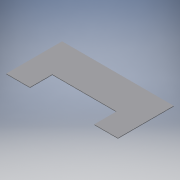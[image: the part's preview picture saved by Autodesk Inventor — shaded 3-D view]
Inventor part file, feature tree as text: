
AUTODESK INVENTOR PART (.ipt)
format: ipt  version: 2016 (Build 200138000, 138)  size: 108,544 bytes
history: native  units: mm
features: extrude x2, sketch x2
ambient origin geometry x8: Origin, YZ Plane, XZ Plane, XY Plane, X Axis, Y Axis, Z Axis, Center Point
bodies: Solid1 (feature_tree)
feature tree (4):
  extrude  "Extrusion1"  Depth=10.0mm TaperAngle=0.0deg
  extrude  "Extrusion2"  [1 undecoded]
  sketch  "Sketch1"  dims[d4=0.0mm d8=10.0mm d9=0.0mm]
  sketch  "Sketch2"  dims[d10=700.0mm]
note: 1 required parameter value undecoded (feature->parameter linkage not recoverable at this tier; creation-order binding heuristic only, values carry confidence <= 0.55)
